FCSTD DOCUMENT  (FreeCAD 0.21R33771 (Git))
Label: basic-sketcher
License: All rights reserved
LicenseURL: http://en.wikipedia.org/wiki/All_rights_reserved
objects: Sketcher::SketchObject×1
note: 1 computed .brp shape members not serialized (recipe doc carries the construction recipe); baked Part::Feature solids carry a one-line shape summary decoded from their .brp

FEATURE [Sketcher::SketchObject] Sketch
  FullyConstrained = false
  sketch-geometry (11):
    g0: LineSegment StartX=0 StartY=0 StartZ=0 EndX=17.6336 EndY=24.2705 EndZ=0
    g1: LineSegment StartX=0 StartY=0 StartZ=0 EndX=-17.6336 EndY=24.2705 EndZ=0
    g2: LineSegment StartX=0 StartY=0 StartZ=0 EndX=-28.5317 EndY=-9.27051 EndZ=0
    g3: LineSegment StartX=0 StartY=0 StartZ=0 EndX=28.5317 EndY=-9.27051 EndZ=0
    g4: LineSegment StartX=0 StartY=0 StartZ=0 EndX=0 EndY=-30 EndZ=0
    g5: Circle CenterX=0 CenterY=0 CenterZ=0 NormalX=0 NormalY=0 NormalZ=1 AngleXU=0 Radius=8.00567
    g6: ArcOfCircle CenterX=17.6336 CenterY=24.2705 CenterZ=0 NormalX=0 NormalY=0 NormalZ=1 AngleXU=0 Radius=8.01258 StartAngle=5.64765 EndAngle=8.80195
    g7: ArcOfCircle CenterX=-17.6336 CenterY=24.2705 CenterZ=0 NormalX=0 NormalY=0 NormalZ=1 AngleXU=0 Radius=8.04803 StartAngle=0.696729 EndAngle=3.84067
    g8: ArcOfCircle CenterX=28.5317 CenterY=-9.27051 CenterZ=0 NormalX=0 NormalY=0 NormalZ=1 AngleXU=0 Radius=8.08876 StartAngle=4.40299 EndAngle=7.54451
    g9: ArcOfCircle CenterX=0 CenterY=-30 CenterZ=0 NormalX=0 NormalY=0 NormalZ=1 AngleXU=0 Radius=7.99644 StartAngle=3.13577 EndAngle=6.28192
    g10: ArcOfCircle CenterX=-28.5317 CenterY=-9.27051 CenterZ=0 NormalX=0 NormalY=0 NormalZ=1 AngleXU=0 Radius=7.99806 StartAngle=1.93501 EndAngle=5.07616
  constraints (21):
    c: Coincident(g0,g-1)
    c: Coincident(g1,g0)
    c: Coincident(g2,g0)
    c: Coincident(g3,g0)
    c: Coincident(g4,g0)
    c: PointOnObject(g4,g-2)
    c: Equal(g0,g1)
    c: Equal(g1,g2)
    c: Equal(g2,g3)
    c: Equal(g3,g4)
    c: DistanceY(g4,g4) = 30
    c: Angle(g4,g3) = 1.25664
    c: Angle(g3,g0) = 1.25664
    c: Angle(g0,g1) = 1.25664
    c: Angle(g1,g2) = 1.25664
    c: Coincident(g5,g0)
    c: Coincident(g6,g0)
    c: Coincident(g7,g1)
    c: Coincident(g8,g3)
    c: Coincident(g9,g4)
    c: Coincident(g10,g2)
